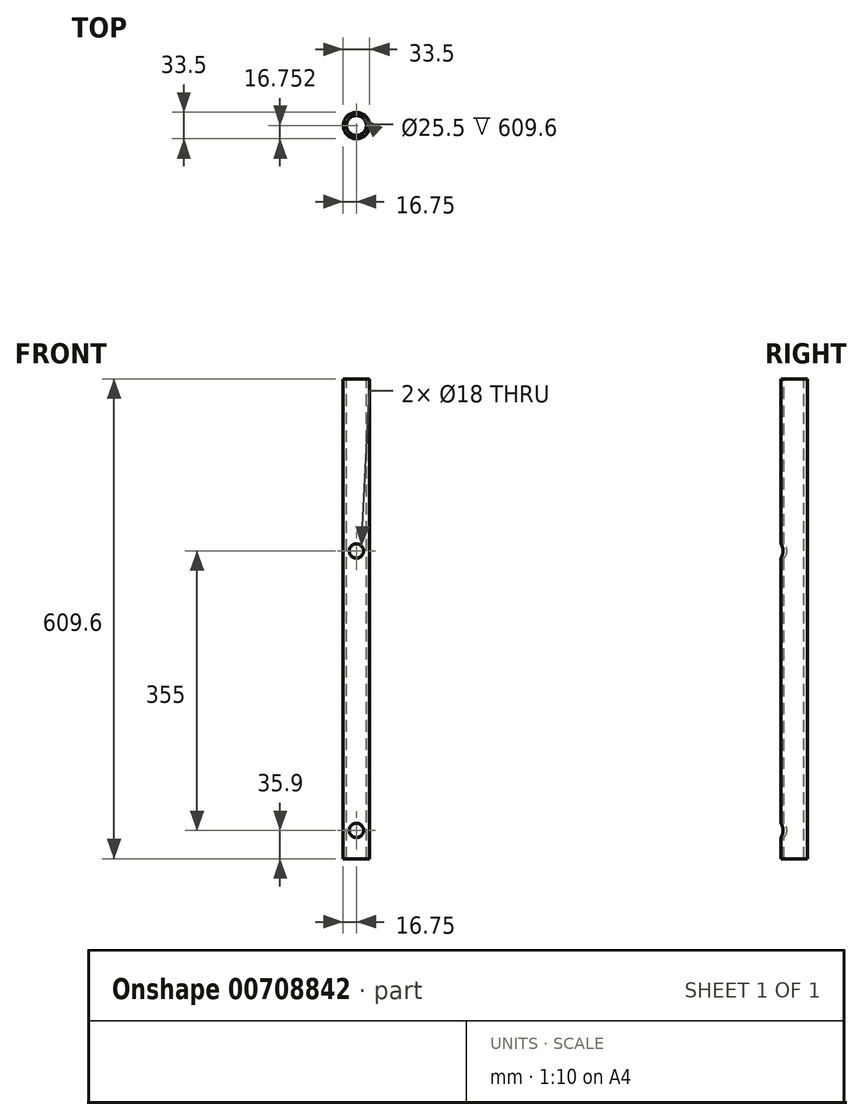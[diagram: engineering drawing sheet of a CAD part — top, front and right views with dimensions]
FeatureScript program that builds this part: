
annotation { "Feature Type Name" : "Feature", "Feature Type Description" : "" }
export const myFeature = defineFeature(function(context is Context, id is Id, definition is map)
    precondition{}
    {
        {
            var Q0;
            Q0=qCreatedBy(makeId("Right.planeOp"),FACE);
            var sketch = newSketch(context, id + "F0", { "sketchPlane" : qUnion([Q0])});
            skLineSegment(sketch, "E0.bottom", {"start": v(12.72, 318.7) * mm, "end": v(16.72, 318.7) * mm});
            skLineSegment(sketch, "E0.top", {"start": v(12.72, -290.9) * mm, "end": v(16.72, -290.9) * mm});
            skLineSegment(sketch, "E0.left", {"start": v(12.72, 318.7) * mm, "end": v(12.72, -290.9) * mm});
            skLineSegment(sketch, "E0.right", {"start": v(16.72, 318.7) * mm, "end": v(16.72, -290.9) * mm});
            skLineSegment(sketch, "E1", {"start": v(-0.03, 318.7) * mm, "end": v(-0.03, -290.9) * mm});
            skSolve(sketch);
        }
        {
            var Q0;
            Q0=makeQuery(id+"F0.imprint","IMPRINT",FACE,{"disambiguationData":[TD([[makeQuery(id+"F0.imprint","IMPRINT",EDGE,{"derivedFrom":sQuery(id+"F0.wireOp",EDGE,"E0.bottom")}),-1.0]])]});
            var Q1;
            Q1=sQuery(id+"F0.wireOp",EDGE,"E1");
            revolve(context, id + "F1", {"surfaceOperationType" : NewSurfaceOperationType.NEW, "entities" : qUnion([Q0]), "axis" : qUnion([Q1]), "revolveType" : RevolveType.FULL});
        }
        {
            var Q0;
            Q0=qCreatedBy(makeId("Front.planeOp"),FACE);
            var sketch = newSketch(context, id + "F2", { "sketchPlane" : qUnion([Q0])});
            skCircle(sketch, "E2", {"center": v(0, 100) * mm, "radius": 9 * mm});
            skCircle(sketch, "E3", {"center": v(0, -255) * mm, "radius": 9 * mm});
            skSolve(sketch);
        }
        {
            var Q0;
            Q0 = qSketchRegion(id + "F2", true);
            extrude(context, id + "F3", {"entities" : qUnion([Q0]), "operationType" : NewBodyOperationType.REMOVE, "endBound" : BoundingType.THROUGH_ALL, "depth" : 0 * mm, "offsetDistance" : 25 * mm});
        }
    });
